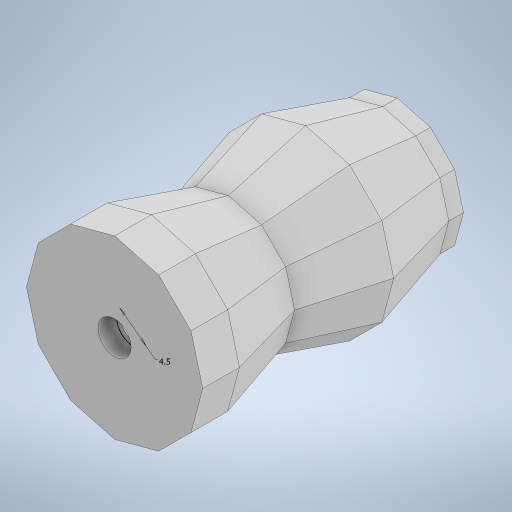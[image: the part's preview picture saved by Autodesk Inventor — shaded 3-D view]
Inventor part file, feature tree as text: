
AUTODESK INVENTOR PART (.ipt)
format: ipt  version: 2023 (Build 270158000, 158)  size: 346,624 bytes
history: native  units: in
note: dims shown in document units (in); Inventor stores cm internally (conversion verified against a paired STEP export)
features: sketch x7, extrude x4, projected_geometry x3, other x2, mirror x2, loft x1, shell x1
ambient origin geometry x8: Origin, YZ Plane, XZ Plane, XY Plane, X Axis, Y Axis, Z Axis, Center Point
bodies: Body1 (feature_tree)
feature tree (20):
  other  "솔리드1"
  sketch  "스케치1"
  other  "작업 평면1"
  loft  "로프트1"
  mirror  "미러1"
  mirror  "미러2"
  extrude  "돌출1"  Depth=0.4134in
  sketch  "스케치4"
  shell  "쉘1"  Thickness=0.7087in
  extrude  "돌출2"  TaperAngle=0.0deg  [1 undecoded]
  extrude  "돌출3"  TaperAngle=0.0deg  [1 undecoded]
  extrude  "돌출4"  Depth=0.0984in TaperAngle=0.0deg
  sketch  "스케치2"
  sketch  "스케치3"
  projected_geometry  "투영된 루프1"
  sketch  "스케치5"
  projected_geometry  "투영된 루프2"
  sketch  "스케치6"
  sketch  "스케치7"
  projected_geometry  "투영된 루프3"
note: 2 required parameter values undecoded (feature->parameter linkage not recoverable at this tier; creation-order binding heuristic only, values carry confidence <= 0.55)
